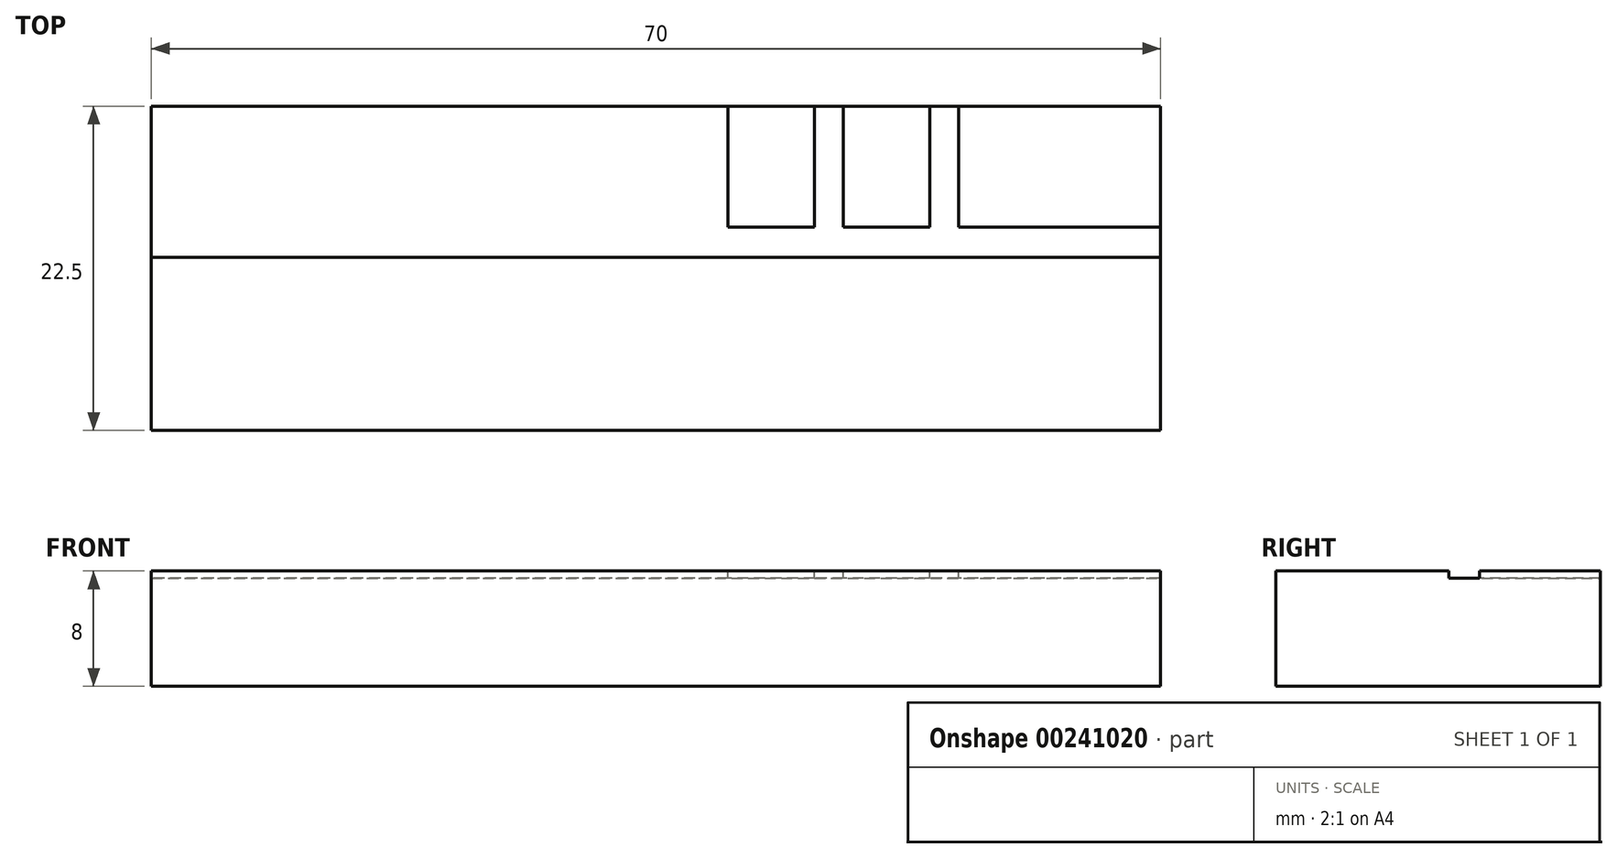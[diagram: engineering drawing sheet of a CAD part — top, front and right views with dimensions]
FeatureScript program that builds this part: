
annotation { "Feature Type Name" : "Feature", "Feature Type Description" : "" }
export const myFeature = defineFeature(function(context is Context, id is Id, definition is map)
    precondition{}
    {
        {
            var Q0;
            Q0=qCreatedBy(makeId("Top.planeOp"),FACE);
            var sketch = newSketch(context, id + "F0", { "sketchPlane" : qUnion([Q0])});
            skLineSegment(sketch, "E0.bottom", {"start": v(35, -11.25) * mm, "end": v(-35, -11.25) * mm});
            skLineSegment(sketch, "E0.top", {"start": v(35, 11.25) * mm, "end": v(-35, 11.25) * mm});
            skLineSegment(sketch, "E0.left", {"start": v(35, -11.25) * mm, "end": v(35, 11.25) * mm});
            skLineSegment(sketch, "E0.right", {"start": v(-35, -11.25) * mm, "end": v(-35, 11.25) * mm});
            skPoint(sketch, "E0.middle", {"position": v(0, 0) * mm});
            skLineSegment(sketch, "E1.bottom", {"start": v(-35, -0.75) * mm, "end": v(35, -0.75) * mm});
            skLineSegment(sketch, "E1.top", {"start": v(-35, 0.75) * mm, "end": v(35, 0.75) * mm});
            skLineSegment(sketch, "E1.left", {"start": v(-35, -0.75) * mm, "end": v(-35, 0.75) * mm});
            skLineSegment(sketch, "E1.right", {"start": v(35, -0.75) * mm, "end": v(35, 0.75) * mm});
            skLineSegment(sketch, "E2", {"start": v(-32, -11.25) * mm, "end": v(-32, -0.75) * mm});
            skLineSegment(sketch, "E3", {"start": v(-26, -11.25) * mm, "end": v(-26, -0.75) * mm});
            skLineSegment(sketch, "E4", {"start": v(-24, -11.25) * mm, "end": v(-24, -0.75) * mm});
            skLineSegment(sketch, "E5.1.0.1", {"start": v(-18, -11.25) * mm, "end": v(-18, -0.75) * mm});
            skLineSegment(sketch, "E5.1.0.2", {"start": v(-16, -11.25) * mm, "end": v(-16, -0.75) * mm});
            skLineSegment(sketch, "E5.2.0.0", {"start": v(-16, -11.25) * mm, "end": v(-16, -0.75) * mm});
            skLineSegment(sketch, "E5.2.0.1", {"start": v(-10, -11.25) * mm, "end": v(-10, -0.75) * mm});
            skLineSegment(sketch, "E5.2.0.2", {"start": v(-8, -11.25) * mm, "end": v(-8, -0.75) * mm});
            skLineSegment(sketch, "E5.3.0.0", {"start": v(-8, -11.25) * mm, "end": v(-8, -0.75) * mm});
            skLineSegment(sketch, "E5.3.0.1", {"start": v(-2, -11.25) * mm, "end": v(-2, -0.75) * mm});
            skLineSegment(sketch, "E5.3.0.2", {"start": v(0, -11.25) * mm, "end": v(0, -0.75) * mm});
            skLineSegment(sketch, "E5.4.0.0", {"start": v(0, -11.25) * mm, "end": v(0, -0.75) * mm});
            skLineSegment(sketch, "E5.4.0.1", {"start": v(6, -11.25) * mm, "end": v(6, -0.75) * mm});
            skLineSegment(sketch, "E5.4.0.2", {"start": v(8, -11.25) * mm, "end": v(8, -0.75) * mm});
            skLineSegment(sketch, "E5.5.0.0", {"start": v(8, -11.25) * mm, "end": v(8, -0.75) * mm});
            skLineSegment(sketch, "E5.5.0.1", {"start": v(14, -11.25) * mm, "end": v(14, -0.75) * mm});
            skLineSegment(sketch, "E5.5.0.2", {"start": v(16, -11.25) * mm, "end": v(16, -0.75) * mm});
            skLineSegment(sketch, "E5.6.0.0", {"start": v(16, -11.25) * mm, "end": v(16, -0.75) * mm});
            skLineSegment(sketch, "E5.6.0.1", {"start": v(22, -11.25) * mm, "end": v(22, -0.75) * mm});
            skLineSegment(sketch, "E5.6.0.2", {"start": v(24, -11.25) * mm, "end": v(24, -0.75) * mm});
            skLineSegment(sketch, "E5.7.0.0", {"start": v(24, -11.25) * mm, "end": v(24, -0.75) * mm});
            skLineSegment(sketch, "E5.7.0.1", {"start": v(30, -11.25) * mm, "end": v(30, -0.75) * mm});
            skLineSegment(sketch, "E5.direction1", {"start": v(-32, -11.25) * mm, "end": v(-24, -11.25) * mm, "construction": true});
            skPoint(sketch, "E6.middle", {"position": v(3, 0) * mm});
            skLineSegment(sketch, "E7", {"start": v(35.01, 11.13) * mm, "end": v(35.01, 0.75) * mm});
            skLineSegment(sketch, "E8", {"start": v(29.01, 11.25) * mm, "end": v(29.01, 2.87) * mm});
            skLineSegment(sketch, "E9", {"start": v(27.01, 11.25) * mm, "end": v(27.01, 2.87) * mm});
            skLineSegment(sketch, "E10.1.0.1", {"start": v(21, 11.25) * mm, "end": v(21, 2.87) * mm});
            skLineSegment(sketch, "E10.1.0.2", {"start": v(19, 11.25) * mm, "end": v(19, 2.87) * mm});
            skLineSegment(sketch, "E10.2.0.1", {"start": v(13, 11.25) * mm, "end": v(13, 2.87) * mm});
            skLineSegment(sketch, "E10.2.0.2", {"start": v(11, 11.25) * mm, "end": v(11, 2.87) * mm});
            skLineSegment(sketch, "E10.3.0.1", {"start": v(5, 11.25) * mm, "end": v(5, 2.87) * mm});
            skLineSegment(sketch, "E10.3.0.2", {"start": v(3, 11.25) * mm, "end": v(3, 2.87) * mm});
            skLineSegment(sketch, "E10.4.0.0", {"start": v(3, 11.25) * mm, "end": v(3, 2.87) * mm});
            skLineSegment(sketch, "E10.4.0.1", {"start": v(-3, 11.25) * mm, "end": v(-3, 2.87) * mm});
            skLineSegment(sketch, "E10.4.0.2", {"start": v(-5, 11.25) * mm, "end": v(-5, 2.87) * mm});
            skLineSegment(sketch, "E10.5.0.0", {"start": v(-5, 11.25) * mm, "end": v(-5, 2.87) * mm});
            skLineSegment(sketch, "E10.5.0.1", {"start": v(-11, 11.25) * mm, "end": v(-11, 2.87) * mm});
            skLineSegment(sketch, "E10.5.0.2", {"start": v(-13, 11.25) * mm, "end": v(-13, 2.87) * mm});
            skLineSegment(sketch, "E10.6.0.0", {"start": v(-13, 11.25) * mm, "end": v(-13, 2.87) * mm});
            skLineSegment(sketch, "E10.6.0.1", {"start": v(-19, 11.25) * mm, "end": v(-19, 2.87) * mm});
            skLineSegment(sketch, "E10.6.0.2", {"start": v(-21, 11.25) * mm, "end": v(-21, 2.87) * mm});
            skLineSegment(sketch, "E10.7.0.0", {"start": v(-21, 11.25) * mm, "end": v(-21, 2.87) * mm});
            skLineSegment(sketch, "E10.7.0.1", {"start": v(-27, 11.25) * mm, "end": v(-27, 2.87) * mm});
            skLineSegment(sketch, "E11", {"start": v(35.01, 2.87) * mm, "end": v(-27, 2.87) * mm});
            skLineSegment(sketch, "E12.trimOffspring", {"start": v(-27, 0.75) * mm, "end": v(-27, 0.75) * mm});
            skLineSegment(sketch, "E13.trimOffspring", {"start": v(-21, 0.75) * mm, "end": v(-21, 0.75) * mm});
            skLineSegment(sketch, "E14.trimOffspring", {"start": v(-19, 0.75) * mm, "end": v(-19, 0.75) * mm});
            skLineSegment(sketch, "E15.trimOffspring", {"start": v(-13, 0.75) * mm, "end": v(-13, 0.75) * mm});
            skLineSegment(sketch, "E16.trimOffspring", {"start": v(-11, 0.75) * mm, "end": v(-11, 0.75) * mm});
            skLineSegment(sketch, "E17.trimOffspring", {"start": v(-5, 0.75) * mm, "end": v(-5, 0.75) * mm});
            skLineSegment(sketch, "E18.trimOffspring", {"start": v(-3, 0.75) * mm, "end": v(-3, 0.75) * mm});
            skLineSegment(sketch, "E19.trimOffspring", {"start": v(3, 0.75) * mm, "end": v(3, 0.75) * mm});
            skLineSegment(sketch, "E20.trimOffspring", {"start": v(5, 0.75) * mm, "end": v(5, 0.75) * mm});
            skLineSegment(sketch, "E21.trimOffspring", {"start": v(11, 0.75) * mm, "end": v(11, 0.75) * mm});
            skLineSegment(sketch, "E22.trimOffspring", {"start": v(13, 0.75) * mm, "end": v(13, 0.75) * mm});
            skLineSegment(sketch, "E23.trimOffspring", {"start": v(19, 0.75) * mm, "end": v(19, 0.75) * mm});
            skLineSegment(sketch, "E24.trimOffspring", {"start": v(21, 0.75) * mm, "end": v(21, 0.75) * mm});
            skLineSegment(sketch, "E25.trimOffspring", {"start": v(27.01, 0.75) * mm, "end": v(27.01, 0.75) * mm});
            skLineSegment(sketch, "E26.trimOffspring", {"start": v(29.01, 0.75) * mm, "end": v(29.01, 0.75) * mm});
            skSolve(sketch);
        }
        {
            var Q0;
            Q0 = qSketchRegion(id + "F0", true);
            extrude(context, id + "F1", {"entities" : qUnion([Q0]), "oppositeDirection" : true, "depth" : 8 * mm});
        }
        {
            var Q0;
            {var subQ9=sQuery(id+"F0.wireOp",EDGE,"E10.3.0.1");Q0=makeQuery(id+"F0.imprint","IMPRINT",FACE,{"disambiguationData":[TD([[makeQuery(id+"F0.imprint","IMPRINT",EDGE,{"derivedFrom":subQ9}),-1.0]])]});}
            var Q1;
            {var subQ0=sQuery(id+"F0.wireOp",EDGE,"E10.2.0.1");Q1=makeQuery(id+"F0.imprint","IMPRINT",FACE,{"disambiguationData":[TD([[makeQuery(id+"F0.imprint","IMPRINT",EDGE,{"derivedFrom":subQ0}),-1.0]])]});}
            var Q2;
            {var subQ0=sQuery(id+"F0.wireOp",EDGE,"E10.1.0.1");Q2=makeQuery(id+"F0.imprint","IMPRINT",FACE,{"disambiguationData":[TD([[makeQuery(id+"F0.imprint","IMPRINT",EDGE,{"derivedFrom":subQ0}),-1.0]])]});}
            extrude(context, id + "F2", {"entities" : qUnion([Q0, Q1, Q2]), "operationType" : NewBodyOperationType.REMOVE, "oppositeDirection" : true, "depth" : .5 * mm});
        }
    });
